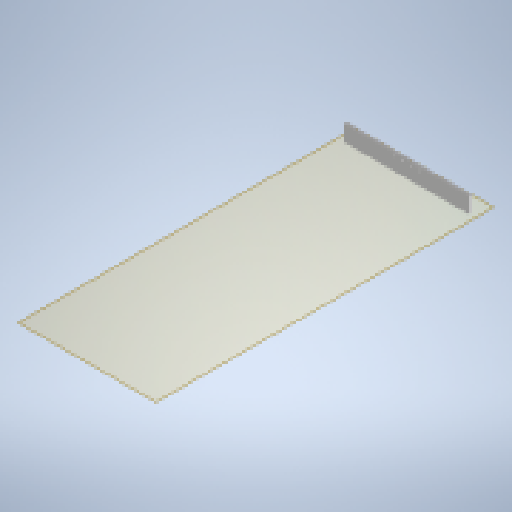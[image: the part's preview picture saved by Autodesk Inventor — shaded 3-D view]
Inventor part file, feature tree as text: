
AUTODESK INVENTOR PART (.ipt)
format: ipt  version: 2025 (Build 290162010, 162A)  size: 149,504 bytes
history: native  units: mm
features: other x3, sketch x2, plane x1, extrude x1, hole x1, reference x1
ambient origin geometry x8: Origin, YZ Plane, XZ Plane, XY Plane, X Axis, Y Axis, Z Axis, Center Point
bodies: Volumenkörper1 (feature_tree)
feature tree (9):
  plane  "Arbeitsebene1"
  extrude  "Extrusion1"  Depth=25.0mm TaperAngle=0.0deg
  hole  "Bohrung1"  [1 undecoded]
  sketch  "Skizze1"  dims[d0=5.0mm d1=25.0mm d2=0.0mm]
  reference  "Referenz1"
  sketch  "Skizze2"  dims[d3=3.0mm d4=8.0mm d5=4.0mm d6=2.0mm d7=90.0deg d8=10.0mm d9=20.594885mm d10=0.5mm d11=0.872665mm d12=0.5mm d13=0.872665mm]
  other  "<userpath>\Documents\Inventor\Krandemonstrator\Demonstrator.iam"
  other  "Demonstrator.iam"
  other  "FrameSide:1"
note: 1 required parameter value undecoded (feature->parameter linkage not recoverable at this tier; creation-order binding heuristic only, values carry confidence <= 0.55)
